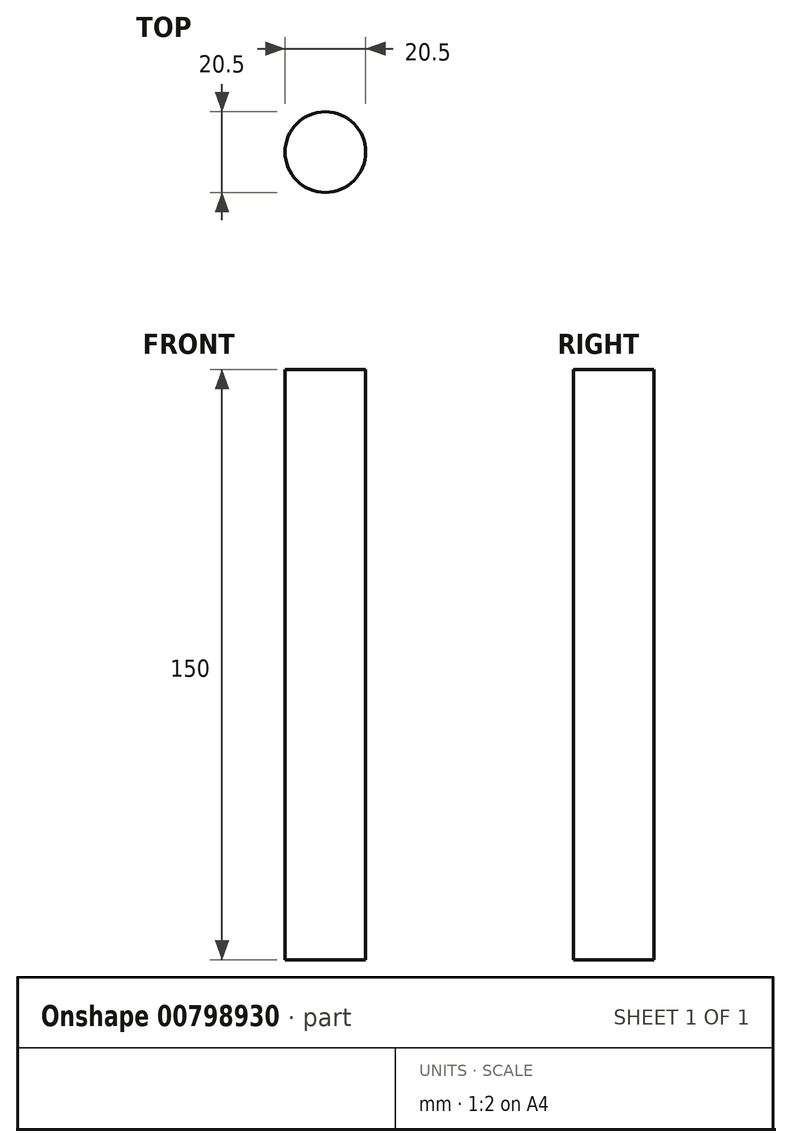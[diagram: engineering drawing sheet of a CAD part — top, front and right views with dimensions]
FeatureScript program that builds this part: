
annotation { "Feature Type Name" : "Feature", "Feature Type Description" : "" }
export const myFeature = defineFeature(function(context is Context, id is Id, definition is map)
    precondition{}
    {
        {
            var Q0;
            Q0=qCreatedBy(makeId("Top.planeOp"),FACE);
            var sketch = newSketch(context, id + "F0", { "sketchPlane" : qUnion([Q0])});
            skCircle(sketch, "E0", {"center": v(0, 0) * mm, "radius": 10.25 * mm});
            skSolve(sketch);
        }
        {
            var Q0;
            Q0=makeQuery(id+"F0.imprint","IMPRINT",FACE,{"disambiguationData":[TD([[makeQuery(id+"F0.imprint","IMPRINT",EDGE,{"derivedFrom":sQuery(id+"F0.wireOp",EDGE,"E0")}),1.0]])]});
            extrude(context, id + "F1", {"entities" : qUnion([Q0]), "depth" : 150 * mm, "offsetDistance" : 25 * mm});
        }
    });
